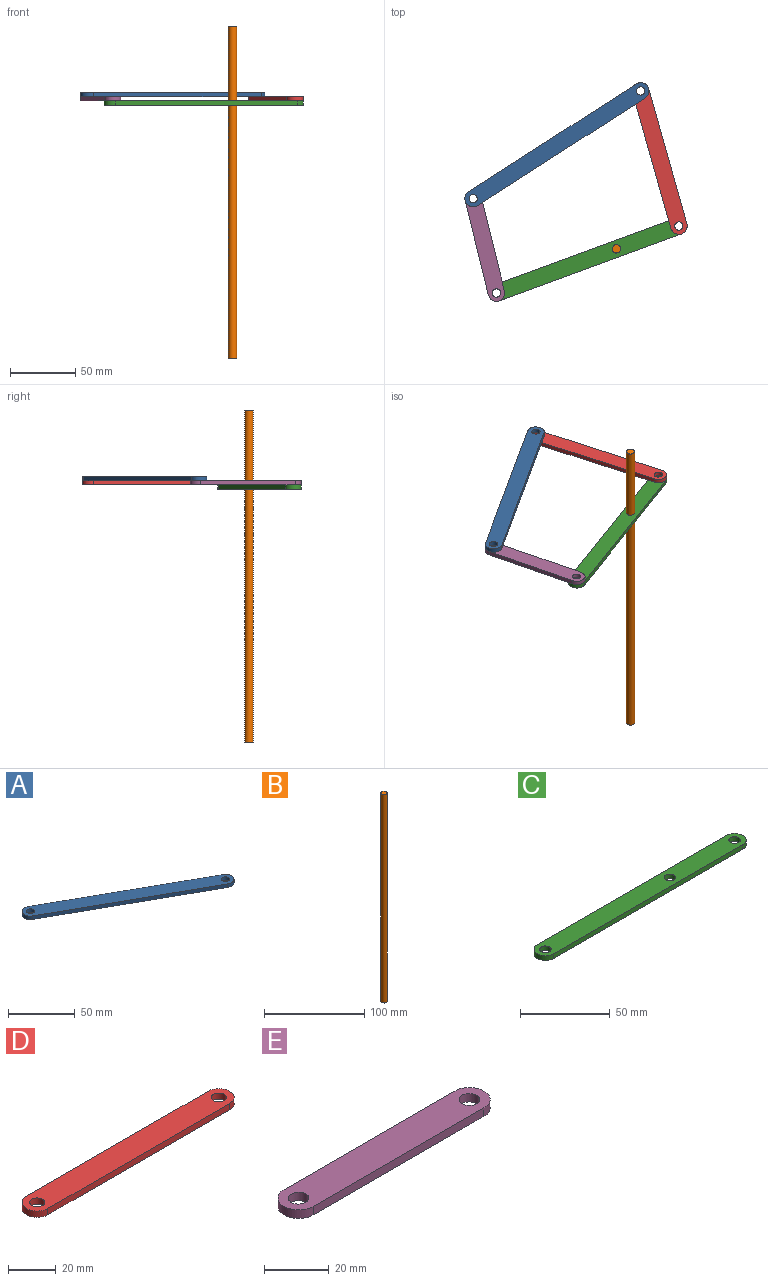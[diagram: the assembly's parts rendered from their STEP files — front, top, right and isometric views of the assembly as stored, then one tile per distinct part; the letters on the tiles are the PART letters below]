
ASSEMBLY  parts=5 mates=5
PART A: 8 faces, bbox 145.8x86.9x3.2 mm
  f0: plane 145.8x86.93mm, normal (0,0,1), area 1998.8mm2, adj f2,f3,f4,f5,f6,f7
  f1: plane 145.8x86.93mm, normal (0,0,-1), area 1998.8mm2, adj f2,f3,f4,f5,f6,f7
  f2: cylinder r=6.35mm len=11.9mm, axis (0,0,-1), area 63.3mm2, adj f0,f1,f3,f5
  f3: plane 133.1x74.23mm, normal (-0.49,-0.87,0), area 483.9mm2, adj f0,f1,f2,f4
  f4: cylinder r=6.35mm len=11.9mm, axis (0,0,-1), area 63.3mm2, adj f0,f1,f3,f5
  f5: plane 133.1x74.23mm, normal (0.49,0.87,0), area 483.9mm2, adj f0,f1,f2,f4
  f6: cylinder r=3.17mm len=6.35mm, axis (0,0,-1), area 63.3mm2, adj f0,f1
  f7: cylinder r=3.17mm len=6.35mm, axis (0,0,-1), area 63.3mm2, adj f0,f1
PART B: 3 faces, bbox 6.4x6.4x254 mm
  f0: cylinder r=3.17mm len=254mm, axis (0,0,-1), area 5067.1mm2, adj f1,f2
  f1: plane 6.35x6.35mm, normal (0,0,1), area 31.7mm2, adj f0
  f2: plane 6.35x6.35mm, normal (0,0,-1), area 31.7mm2, adj f0
PART C: 9 faces, bbox 161.4x12.7x3.2 mm
  f0: plane 161.38x12.7mm, normal (0,0,1), area 1919.9mm2, adj f2,f3,f4,f5,f6,f7,f8
  f1: plane 161.38x12.7mm, normal (0,0,-1), area 1919.9mm2, adj f2,f3,f4,f5,f6,f7,f8
  f2: cylinder r=6.35mm len=12.7mm, axis (0,0,-1), area 63.3mm2, adj f0,f1,f3,f5
  f3: plane 148.68x3.18mm, normal (0,-1,0), area 472.1mm2, adj f0,f1,f2,f4
  f4: cylinder r=6.35mm len=12.7mm, axis (0,0,-1), area 63.3mm2, adj f0,f1,f3,f5
  f5: plane 148.68x3.18mm, normal (0,1,0), area 472.1mm2, adj f0,f1,f2,f4
  f6: cylinder r=3.17mm len=6.35mm, axis (0,0,-1), area 63.3mm2, adj f0,f1
  f7: cylinder r=3.17mm len=6.35mm, axis (0,0,-1), area 63.3mm2, adj f0,f1
  f8: cylinder r=3.17mm len=6.35mm, axis (0,0,-1), area 63.3mm2, adj f0,f1
PART D: 8 faces, bbox 120.1x12.7x3.2 mm
  f0: plane 120.08x12.7mm, normal (0,0,1), area 1427.1mm2, adj f2,f3,f4,f5,f6,f7
  f1: plane 120.08x12.7mm, normal (0,0,-1), area 1427.1mm2, adj f2,f3,f4,f5,f6,f7
  f2: cylinder r=6.35mm len=12.7mm, axis (0,0,-1), area 63.3mm2, adj f0,f1,f3,f5
  f3: plane 107.38x3.18mm, normal (0,-1,0), area 340.9mm2, adj f0,f1,f2,f4
  f4: cylinder r=6.35mm len=12.7mm, axis (0,0,-1), area 63.3mm2, adj f0,f1,f3,f5
  f5: plane 107.38x3.18mm, normal (0,1,0), area 340.9mm2, adj f0,f1,f2,f4
  f6: cylinder r=3.17mm len=6.35mm, axis (0,0,-1), area 63.3mm2, adj f0,f1
  f7: cylinder r=3.17mm len=6.35mm, axis (0,0,-1), area 63.3mm2, adj f0,f1
PART E: 8 faces, bbox 87x12.7x3.2 mm
  f0: plane 87.04x12.7mm, normal (0,0,1), area 1007.5mm2, adj f2,f3,f4,f5,f6,f7
  f1: plane 87.04x12.7mm, normal (0,0,-1), area 1007.5mm2, adj f2,f3,f4,f5,f6,f7
  f2: cylinder r=6.35mm len=12.7mm, axis (0,0,-1), area 63.3mm2, adj f0,f1,f3,f5
  f3: plane 74.34x3.18mm, normal (0,-1,0), area 236mm2, adj f0,f1,f2,f4
  f4: cylinder r=6.35mm len=12.7mm, axis (0,0,-1), area 63.3mm2, adj f0,f1,f3,f5
  f5: plane 74.34x3.18mm, normal (0,1,0), area 236mm2, adj f0,f1,f2,f4
  f6: cylinder r=3.17mm len=6.35mm, axis (0,0,-1), area 63.3mm2, adj f0,f1
  f7: cylinder r=3.17mm len=6.35mm, axis (0,0,-1), area 63.3mm2, adj f0,f1
PLACE A rot(axis=(0,0,-1),118.1deg) t=(10.25,6.27,74.71)mm fixed
PLACE B rot(axis=(0,0,1),161.5deg) t=(55.84,-73.37,-125.12)mm
PLACE C rot(axis=(0,0,1),20.2deg) t=(33.75,-81.49,68.36)mm
PLACE D rot(axis=(0,0,1),105.8deg) t=(88.94,-4.18,71.53)mm
PLACE E rot(axis=(0,0,-1),76.1deg) t=(-44.94,-71.03,71.53)mm
MATE revolute D.f4 <-> A.f2  axis (0,0,1) through (74.34,47.49,74.71)mm
MATE revolute E.f2 <-> A.f4  axis (0,0,1) through (-53.84,-34.95,74.71)mm
MATE cylindrical B.f0 <-> C.f8  axis (0,0,-1) through (55.84,-73.37,128.88)mm
MATE revolute C.f2 <-> E.f4  axis (0,0,1) through (-36.04,-107.12,71.53)mm
MATE revolute D.f2 <-> C.f4  axis (0,0,-1) through (103.53,-55.85,71.53)mm
